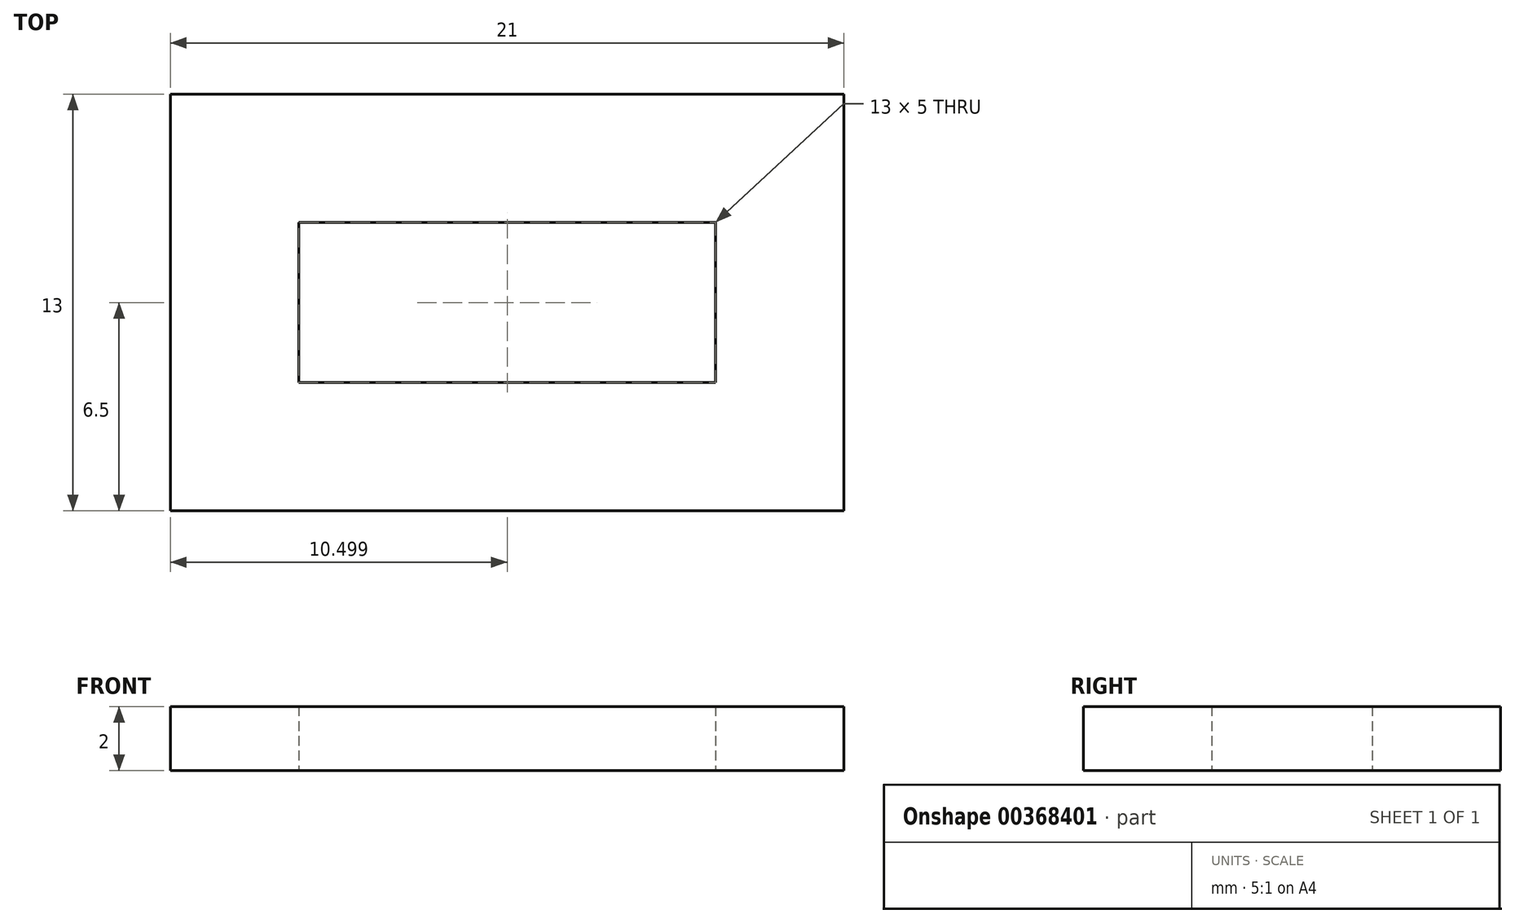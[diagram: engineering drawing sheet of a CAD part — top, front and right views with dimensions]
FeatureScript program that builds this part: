
annotation { "Feature Type Name" : "Feature", "Feature Type Description" : "" }
export const myFeature = defineFeature(function(context is Context, id is Id, definition is map)
    precondition{}
    {
        {
            var Q0;
            Q0=qCreatedBy(makeId("Top.planeOp"),FACE);
            var sketch = newSketch(context, id + "F0", { "sketchPlane" : qUnion([Q0])});
            skLineSegment(sketch, "E0.bottom", {"start": v(-3.57, 5) * mm, "end": v(9.43, 5) * mm});
            skLineSegment(sketch, "E0.top", {"start": v(-3.57, 0) * mm, "end": v(9.43, 0) * mm});
            skLineSegment(sketch, "E0.left", {"start": v(-3.57, 5) * mm, "end": v(-3.57, 0) * mm});
            skLineSegment(sketch, "E0.right", {"start": v(9.43, 5) * mm, "end": v(9.43, 0) * mm});
            skLineSegment(sketch, "E1.bottom", {"start": v(-7.57, 9) * mm, "end": v(13.43, 9) * mm});
            skLineSegment(sketch, "E1.top", {"start": v(-7.57, -4) * mm, "end": v(13.43, -4) * mm});
            skLineSegment(sketch, "E1.left", {"start": v(-7.57, 9) * mm, "end": v(-7.57, -4) * mm});
            skLineSegment(sketch, "E1.right", {"start": v(13.43, 9) * mm, "end": v(13.43, -4) * mm});
            skSolve(sketch);
        }
        {
            var Q0;
            Q0=qSketchRegion(id+"F0",true);
            extrude(context, id + "F1", {"entities" : qUnion([Q0]), "depth" : 2 * mm});
        }
    });
